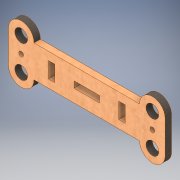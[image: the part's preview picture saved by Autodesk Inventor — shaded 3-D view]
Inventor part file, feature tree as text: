
AUTODESK INVENTOR PART (.ipt)
format: ipt  version: 2019 (Build 230136000, 136)  size: 181,248 bytes
history: native  units: mm
features: sketch x2, other x1, extrude x1, hole x1, projected_geometry x1
ambient origin geometry x8: Origin, YZ Plane, XZ Plane, XY Plane, X Axis, Y Axis, Z Axis, Center Point
bodies: Body1 (feature_tree)
feature tree (6):
  other  "Твердое тело1"
  extrude  "Выдавливание1"  Depth=8.0mm
  hole  "Отверстие1"  [1 undecoded]
  sketch  "Эскиз1"
  sketch  "Эскиз2"
  projected_geometry  "Спроецированная петля1"
note: 1 required parameter value undecoded (feature->parameter linkage not recoverable at this tier; creation-order binding heuristic only, values carry confidence <= 0.55)
